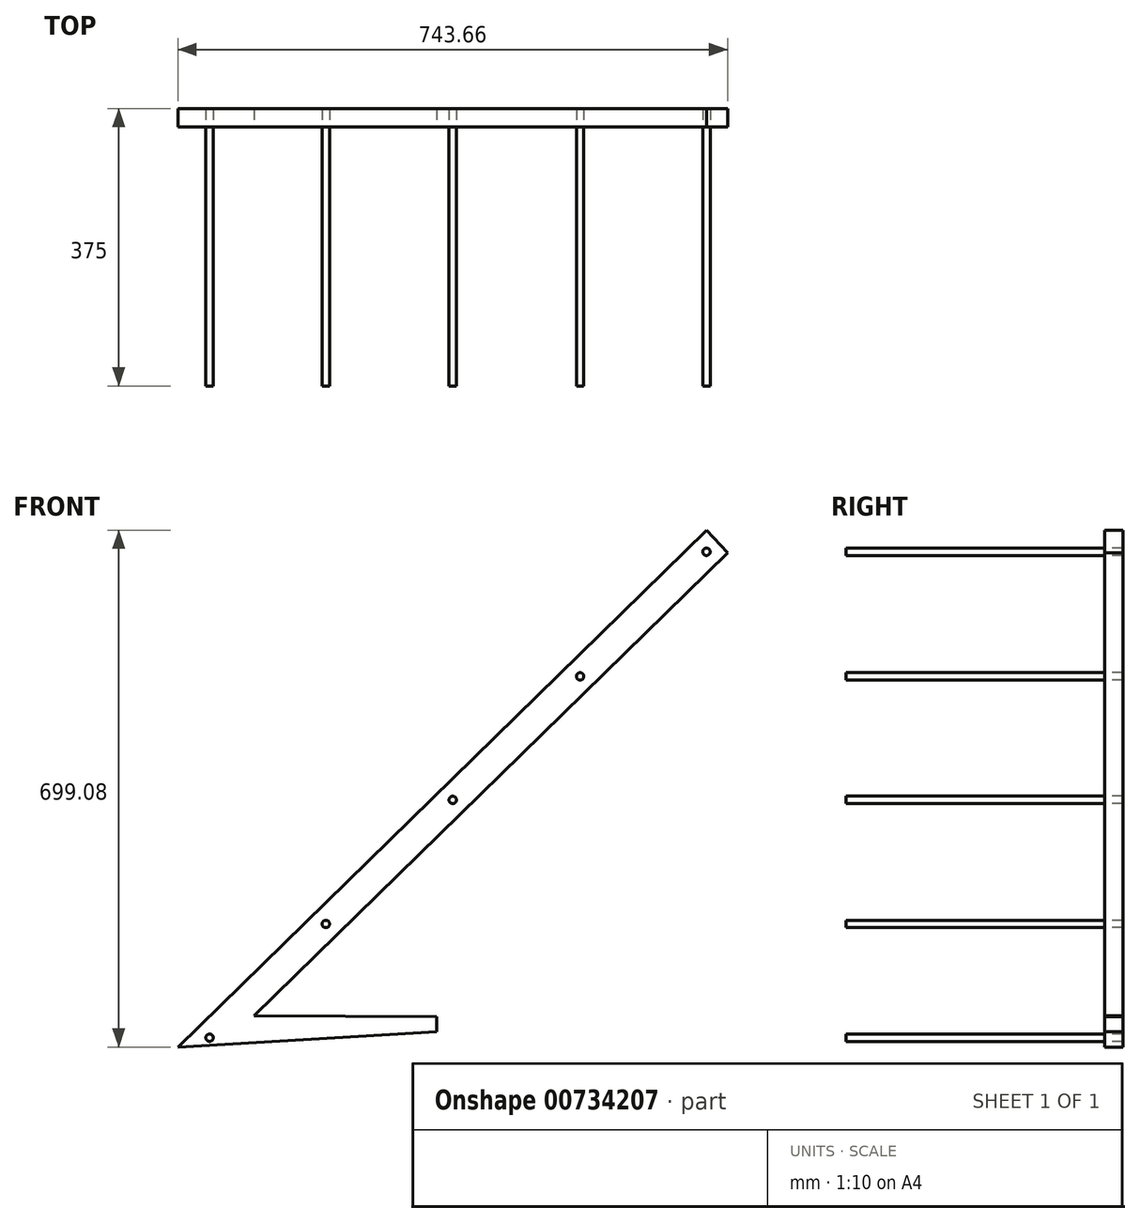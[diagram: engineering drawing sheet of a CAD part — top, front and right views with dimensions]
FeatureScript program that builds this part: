
annotation { "Feature Type Name" : "Feature", "Feature Type Description" : "" }
export const myFeature = defineFeature(function(context is Context, id is Id, definition is map)
    precondition{}
    {
        {
            var Q0;
            Q0=qCreatedBy(makeId("Front.planeOp"),FACE);
            var sketch = newSketch(context, id + "F0", { "sketchPlane" : qUnion([Q0])});
            skPoint(sketch, "E0.1.internal.orphan", {"position": v(350, -1) * mm});
            skLineSegment(sketch, "E1", {"start": v(715.04, 657.08) * mm, "end": v(743.66, 626.34) * mm});
            skLineSegment(sketch, "E2", {"start": v(743.66, 626.34) * mm, "end": v(103.02, 0) * mm});
            skLineSegment(sketch, "E3", {"start": v(103.02, 0) * mm, "end": v(350, -1) * mm});
            skPoint(sketch, "E4.start.orphan", {"position": v(0, 0) * mm});
            skLineSegment(sketch, "E5", {"start": v(0, -42) * mm, "end": v(715.04, 657.08) * mm});
            skLineSegment(sketch, "E6", {"start": v(0, -42) * mm, "end": v(350, -21) * mm});
            skPoint(sketch, "E7.end.orphan", {"position": v(350, -43) * mm});
            skLineSegment(sketch, "E8", {"start": v(350, -1) * mm, "end": v(350, -21) * mm});
            skCircle(sketch, "E9", {"center": v(715.04, 627.73) * mm, "radius": 5 * mm});
            skCircle(sketch, "E10", {"center": v(544.13, 459.24) * mm, "radius": 5 * mm});
            skCircle(sketch, "E11", {"center": v(371.82, 292.18) * mm, "radius": 5 * mm});
            skCircle(sketch, "E12", {"center": v(200.22, 124.39) * mm, "radius": 5 * mm});
            skCircle(sketch, "E13", {"center": v(42.91, -29.41) * mm, "radius": 5 * mm});
            skSolve(sketch);
        }
        {
            var Q0;
            Q0=makeQuery(id+"F0.imprint","IMPRINT",FACE,{"disambiguationData":[TD([[makeQuery(id+"F0.imprint","IMPRINT",EDGE,{"derivedFrom":sQuery(id+"F0.wireOp",EDGE,"E10")}),1.0]])]});
            var Q1;
            Q1=makeQuery(id+"F0.imprint","IMPRINT",FACE,{"disambiguationData":[TD([[makeQuery(id+"F0.imprint","IMPRINT",EDGE,{"derivedFrom":sQuery(id+"F0.wireOp",EDGE,"E9")}),1.0]])]});
            var Q2;
            Q2=makeQuery(id+"F0.imprint","IMPRINT",FACE,{"disambiguationData":[TD([[makeQuery(id+"F0.imprint","IMPRINT",EDGE,{"derivedFrom":sQuery(id+"F0.wireOp",EDGE,"E11")}),1.0]])]});
            var Q3;
            Q3=makeQuery(id+"F0.imprint","IMPRINT",FACE,{"disambiguationData":[TD([[makeQuery(id+"F0.imprint","IMPRINT",EDGE,{"derivedFrom":sQuery(id+"F0.wireOp",EDGE,"E12")}),1.0]])]});
            var Q4;
            Q4=makeQuery(id+"F0.imprint","IMPRINT",FACE,{"disambiguationData":[TD([[makeQuery(id+"F0.imprint","IMPRINT",EDGE,{"derivedFrom":sQuery(id+"F0.wireOp",EDGE,"E13")}),1.0]])]});
            extrude(context, id + "F1", {"entities" : qUnion([Q0, Q1, Q2, Q3, Q4]), "depth" : 350 * mm, "offsetDistance" : 25 * mm});
        }
        {
            var Q0;
            Q0=makeQuery(id+"F0.imprint","IMPRINT",FACE,{"disambiguationData":[TD([[makeQuery(id+"F0.imprint","IMPRINT",EDGE,{"derivedFrom":sQuery(id+"F0.wireOp",EDGE,"E1")}),-1.0]])]});
            extrude(context, id + "F2", {"entities" : qUnion([Q0]), "oppositeDirection" : true, "depth" : 25 * mm, "offsetDistance" : 25 * mm});
        }
    });
